# Revit family: FEDGE2-PDI1500xxFSW
name_source: partatom
category: Leuchten
units: mm (PartAtom-declared; Revit-internal decimal feet)

## family parameters
Basisbauteil = Fläche
Beim Laden mit Abzugskörper schneiden = Nein
Bemaßung runder Anschluss = Durchmesser verwenden
Gemeinsam genutzt = Nein
Lichtquelle = Ja
OmniClass-Nummer = 23.80.70.11
OmniClass-Titel = Luminaries for Internal Lighting
Raumberechnungspunkt = Nein
Teiletyp = Normal

## types (6) — shared parameters
Baugruppenkennzeichen = D5020200
Datei für fotometrisches Netz = FEDGE2-PDI1500NDWS850-0750.IES
Emissionsform beim Rendern sichtbar = Nein
Farbfilter = 16777215
Farbtemperaturverschiebung bei Dämpfen der Lampe = <Keine Auswahl>
Hersteller = RIDI Leuchten GmbH
Lampe = LED
Neigungswinkel = 90.00°
URL = www.ridi.de
Von Breite des Rechtecks ausssenden = 1395 mm
Von Länge des Rechtecks aussenden = 222 mm
brand = RIDI
conformity mark = CE
electrical safety class = 1
height = 22 mm  [stored 0.0721785 ft]
ingress protection (IP) code = IP20
length = 1501 mm
nominal frequency = 50-60Hz
nominal voltage = 230
voltage type (AC, DC, UC) = AC
weight = 8,8
width = 341 mm
zero-valued in all types: Vorgabe-Ansicht

## per-type parameters (varying)
| type | Modell | Scheinlast | rated input power |
| FEDGE2-PDI1500NDFSW830-0700 | 0627635AQ | 55 VA | 55 |
| FEDGE2-PDI1500DAFSW830-0700 | 0637635AQ | 55 VA | 55 |
| FEDGE2-PDI1500NDFSW840-0750 | 0627636AQ | 55 VA | 55 |
| FEDGE2-PDI1500DAFSW840-0750 | 0637636AQ | 50 VA | 50 |
| FEDGE2-PDI1500NDFSW850-0750 | 0627637AQ | 55 VA | 55 |
| FEDGE2-PDI1500DAFSW850-0750 | 0637637AQ | 55 VA | 55 |

note: column(s) folded — value = type name in every type: product name

note: [stored X ft] marks values corroborated as IEEE doubles in the binary element streams (Revit-internal decimal feet)
